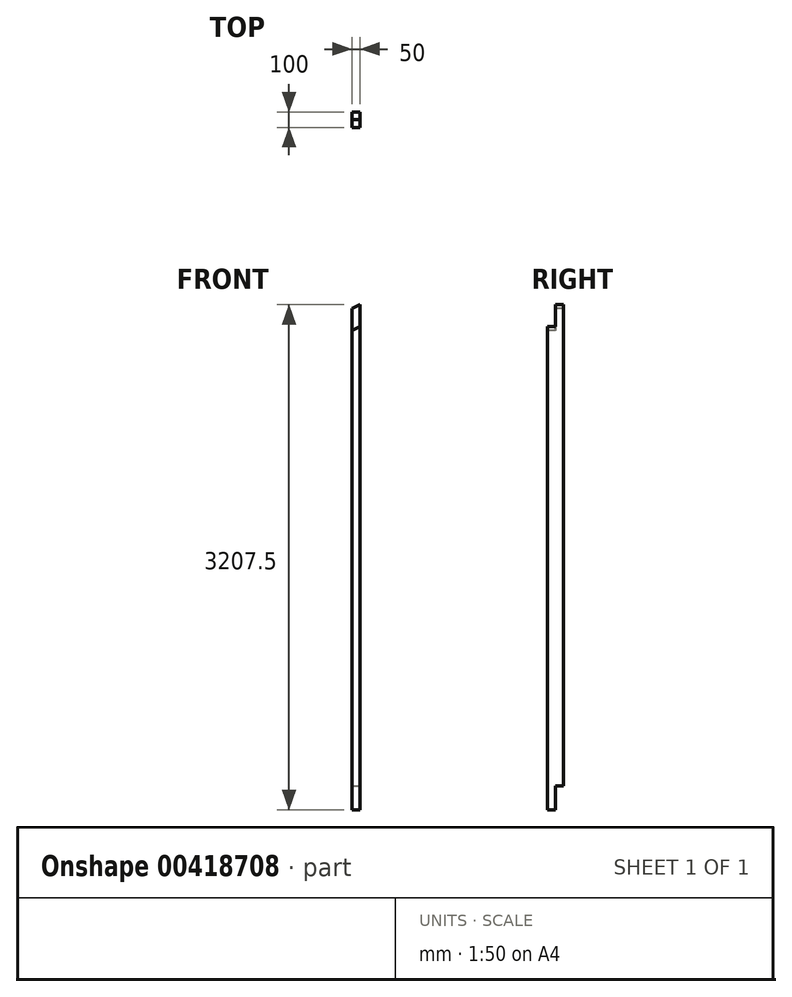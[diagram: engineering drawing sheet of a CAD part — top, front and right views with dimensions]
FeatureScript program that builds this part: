
annotation { "Feature Type Name" : "Feature", "Feature Type Description" : "" }
export const myFeature = defineFeature(function(context is Context, id is Id, definition is map)
    precondition{}
    {
        {
            var Q0;
            Q0=qCreatedBy(makeId("Top.planeOp"),FACE);
            var sketch = newSketch(context, id + "F0", { "sketchPlane" : qUnion([Q0])});
            skLineSegment(sketch, "E0.bottom", {"start": v(-25, 50) * mm, "end": v(25, 50) * mm});
            skLineSegment(sketch, "E0.top", {"start": v(-25, -50) * mm, "end": v(25, -50) * mm});
            skLineSegment(sketch, "E0.left", {"start": v(-25, 50) * mm, "end": v(-25, -50) * mm});
            skLineSegment(sketch, "E0.right", {"start": v(25, 50) * mm, "end": v(25, -50) * mm});
            skPoint(sketch, "E0.middle", {"position": v(0, 0) * mm});
            skSolve(sketch);
        }
        {
            var Q0;
            Q0 = qSketchRegion(id + "F0", true);
            extrude(context, id + "F1", {"entities" : qUnion([Q0]), "depth" : (3210 - 2.5) * mm});
        }
        {
            var Q0;
            Q0=qCreatedBy(makeId("Right.planeOp"),FACE);
            var sketch = newSketch(context, id + "F2", { "sketchPlane" : qUnion([Q0])});
            skLineSegment(sketch, "E1.bottom", {"start": v(50, 0) * mm, "end": v(0, 0) * mm});
            skLineSegment(sketch, "E1.top", {"start": v(50, 150) * mm, "end": v(0, 150) * mm});
            skLineSegment(sketch, "E1.left", {"start": v(50, 0) * mm, "end": v(50, 150) * mm});
            skLineSegment(sketch, "E1.right", {"start": v(0, 0) * mm, "end": v(0, 150) * mm});
            skSolve(sketch);
        }
        {
            var Q0;
            Q0 = qSketchRegion(id + "F2", true);
            extrude(context, id + "F3", {"entities" : qUnion([Q0]), "operationType" : NewBodyOperationType.REMOVE, "endBound" : BoundingType.UP_TO_NEXT, "oppositeDirection" : true, "depth" : 25 * mm, "hasSecondDirection" : true, "secondDirectionBound" : SecondDirectionBoundingType.UP_TO_NEXT, "secondDirectionOppositeDirection" : false, "secondDirectionDepth" : 25 * mm});
        }
        {
            var Q0;
            Q0=makeQuery(id+"F1.opExtrude","SWEPT_FACE",FACE,{"disambiguationData":[OSD([sQuery(id+"F0.wireOp",EDGE,"E0.top")])]});
            var sketch = newSketch(context, id + "F4", { "sketchPlane" : qUnion([Q0])});
            skLineSegment(sketch, "E2", {"start": v(25, 3207.5) * mm, "end": v(-25, 3182.5) * mm});
            skLineSegment(sketch, "E3", {"start": v(-25, 3182.5) * mm, "end": v(-25, 3207.5) * mm});
            skLineSegment(sketch, "E4", {"start": v(-25, 3207.5) * mm, "end": v(25, 3207.5) * mm});
            skSolve(sketch);
        }
        {
            var Q0;
            Q0 = qSketchRegion(id + "F4", true);
            extrude(context, id + "F5", {"entities" : qUnion([Q0]), "operationType" : NewBodyOperationType.REMOVE, "endBound" : BoundingType.UP_TO_NEXT, "oppositeDirection" : true, "depth" : 25 * mm});
        }
        {
            var Q0;
            Q0=makeQuery(id+"F1.opExtrude","SWEPT_FACE",FACE,{"disambiguationData":[OSD([sQuery(id+"F0.wireOp",EDGE,"E0.top")])]});
            var sketch = newSketch(context, id + "F6", { "sketchPlane" : qUnion([Q0])});
            skLineSegment(sketch, "E5", {"start": v(-25, 3042.75) * mm, "end": v(25, 3067.75) * mm});
            skLineSegment(sketch, "E6", {"start": v(25, 3067.75) * mm, "end": v(25, 3207.5) * mm});
            skLineSegment(sketch, "E7", {"start": v(25, 3207.5) * mm, "end": v(-25, 3182.5) * mm});
            skLineSegment(sketch, "E8", {"start": v(-25, 3182.5) * mm, "end": v(-25, 3042.75) * mm});
            skSolve(sketch);
        }
        {
            var Q0;
            Q0 = qSketchRegion(id + "F6", true);
            extrude(context, id + "F7", {"entities" : qUnion([Q0]), "operationType" : NewBodyOperationType.REMOVE, "oppositeDirection" : true, "depth" : 50 * mm});
        }
    });
